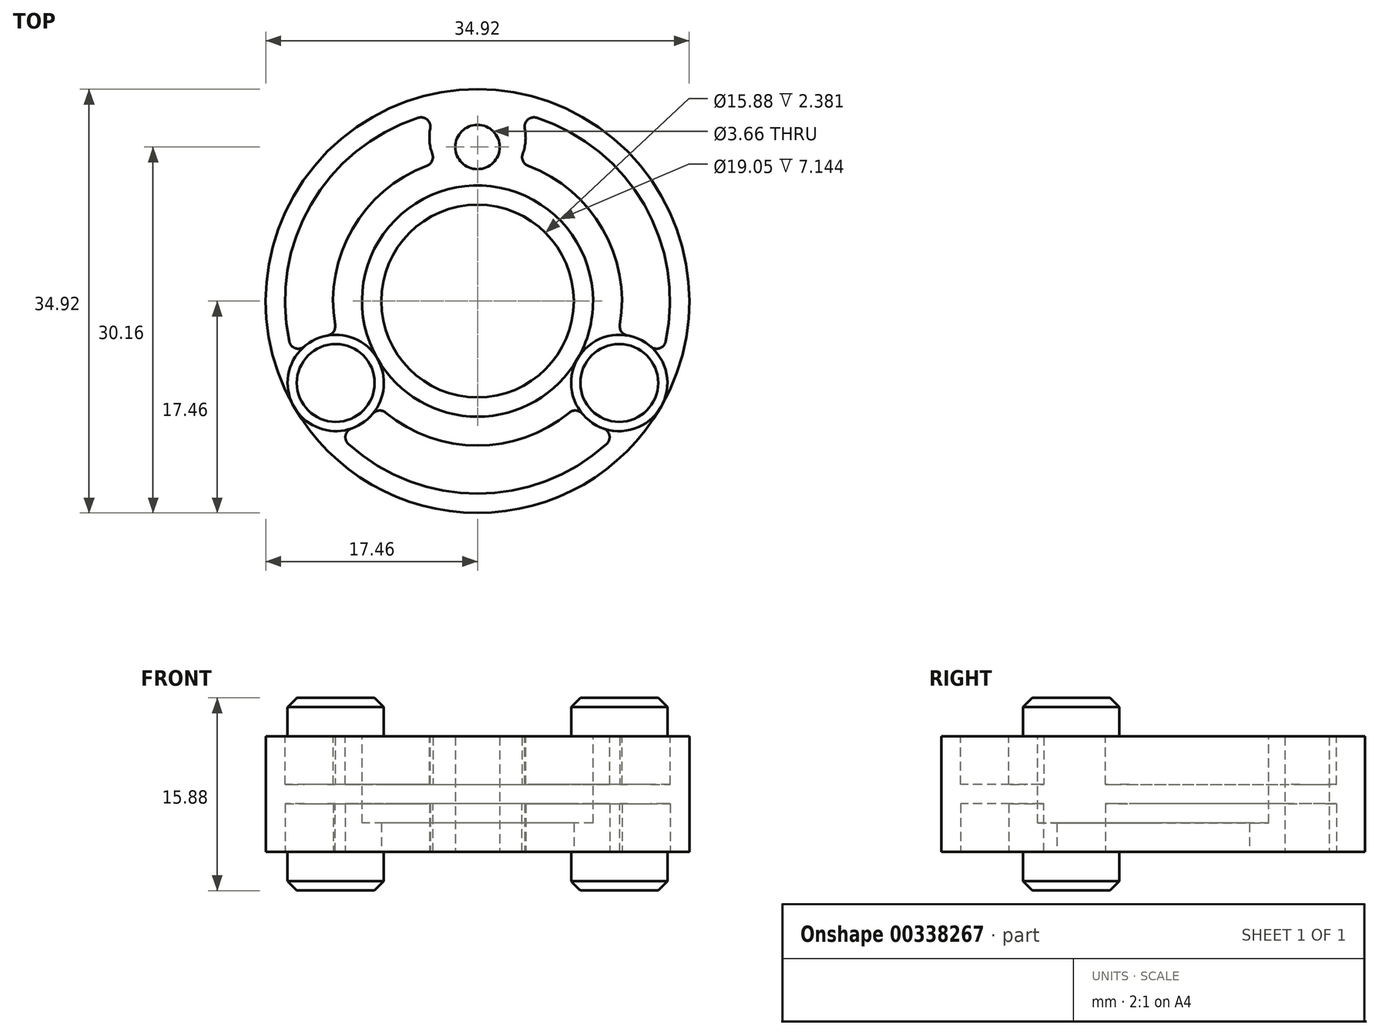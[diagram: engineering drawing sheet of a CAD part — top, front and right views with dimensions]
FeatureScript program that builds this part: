
annotation { "Feature Type Name" : "Feature", "Feature Type Description" : "" }
export const myFeature = defineFeature(function(context is Context, id is Id, definition is map)
    precondition{}
    {
        {
            var Q0;
            Q0=qCreatedBy(makeId("Top.planeOp"),FACE);
            var sketch = newSketch(context, id + "F0", { "sketchPlane" : qUnion([Q0])});
            skCircle(sketch, "E0", {"center": v(0, 0) * mm, "radius": 7.94 * mm});
            skCircle(sketch, "E1", {"center": v(0, 0) * mm, "radius": 17.46 * mm});
            skLineSegment(sketch, "E2", {"start": v(0, 0) * mm, "end": v(0, 12.7) * mm, "construction": true});
            skCircle(sketch, "E3", {"center": v(0, 12.7) * mm, "radius": 4.76 * mm, "construction": true});
            skCircle(sketch, "E4", {"center": v(0, 12.7) * mm, "radius": 1.83 * mm});
            skSolve(sketch);
        }
        {
            var Q0;
            Q0 = qSketchRegion(id + "F0", true);
            extrude(context, id + "F1", {"entities" : qUnion([Q0]), "depth" : 9.52 * mm});
        }
        {
            var Q0;
            Q0=makeQuery(id+"F1.opExtrude","CAP_FACE",FACE,{"disambiguationData":[OSD([sQuery(id+"F0.wireOp",EDGE,"E0"),sQuery(id+"F0.wireOp",EDGE,"E1"),sQuery(id+"F0.wireOp",EDGE,"E4")])],"isStart":false});
            var sketch = newSketch(context, id + "F2", { "sketchPlane" : qUnion([Q0])});
            skCircle(sketch, "E5", {"center": v(0, 0) * mm, "radius": 9.53 * mm});
            skSolve(sketch);
        }
        {
            var Q0;
            Q0 = qSketchRegion(id + "F2", true);
            extrude(context, id + "F3", {"entities" : qUnion([Q0]), "operationType" : NewBodyOperationType.REMOVE, "oppositeDirection" : true, "depth" : 7.14 * mm});
        }
        {
            var Q0;
            {var subQ0=sQuery(id+"F0.wireOp",EDGE,"E1");var subQ1=makeQuery(id+"F1.opExtrude","CAP_FACE",FACE,{"disambiguationData":[OSD([sQuery(id+"F0.wireOp",EDGE,"E0"),subQ0,sQuery(id+"F0.wireOp",EDGE,"E4")])],"isStart":false});Q0=makeQuery(id+"FaGNQa3NOKQJJ3d_1.boolean.opBoolean","SPLIT",FACE,{"disambiguationData":[TD([subQ1,makeQuery(id+"F1.opExtrude","SWEPT_FACE",FACE,{"disambiguationData":[OSD([subQ0])]}),makeQuery(id+"F3.boolean.opBoolean","COPY",FACE,{"derivedFrom":makeQuery(id+"F3.opExtrude","SWEPT_FACE",FACE,{"disambiguationData":[OSD([sQuery(id+"F2.wireOp",EDGE,"E5")])]})}),makeQuery(id+"FaGNQa3NOKQJJ3d_1.opExtrude","SWEPT_FACE",FACE,{"disambiguationData":[OSD([sQuery(id+"FimIUrEkqtjUp3z_1.wireOp",EDGE,"HlGXKecl-ggte-uXjZ-GF2z-oe2yHpBcJ9Dq")])]}),makeQuery(id+"FaGNQa3NOKQJJ3d_1.opExtrude","SWEPT_FACE",FACE,{"disambiguationData":[OSD([sQuery(id+"FimIUrEkqtjUp3z_1.wireOp",EDGE,"b06J7RxP-un1X-OzPm-o8VI-wkIMPVGFyDBE")])]})])],"derivedFrom":subQ1});}
            var sketch = newSketch(context, id + "F4", { "sketchPlane" : qUnion([Q0])});
            skArc(sketch, "E6", {"start": v(-3.42, 15.5) * mm, "mid": v(-3.97, 13.45) * mm, "end": v(-3.38, 11.42) * mm});
            skArc(sketch, "E7", {"start": v(-3.38, 11.42) * mm, "mid": v(-10.31, 5.95) * mm, "end": v(-11.58, -2.78) * mm});
            skArc(sketch, "E8", {"start": v(-3.42, 15.5) * mm, "mid": v(-13.75, 7.94) * mm, "end": v(-15.14, -4.79) * mm});
            skLineSegment(sketch, "E9", {"start": v(0, 0) * mm, "end": v(0, 13.5) * mm, "construction": true});
            skArc(sketch, "E10", {"start": v(-11.58, -2.78) * mm, "mid": v(-13.63, -3.29) * mm, "end": v(-15.14, -4.79) * mm});
            skArc(sketch, "E11", {"start": v(-15.14, -4.79) * mm, "mid": v(-9.74, -10.2) * mm, "end": v(-11.58, -2.78) * mm, "construction": true});
            skLineSegment(sketch, "E12", {"start": v(-11.69, -6.75) * mm, "end": v(0, 0) * mm, "construction": true});
            skSolve(sketch);
        }
        {
            var Q0;
            Q0 = qSketchRegion(id + "F4", true);
            extrude(context, id + "F5", {"entities" : qUnion([Q0]), "operationType" : NewBodyOperationType.REMOVE, "oppositeDirection" : true, "depth" : 3.97 * mm});
        }
        {
            var Q0;
            Q0=makeQuery(id+"F1.opExtrude","CAP_FACE",FACE,{"disambiguationData":[OSD([sQuery(id+"F0.wireOp",EDGE,"E0"),sQuery(id+"F0.wireOp",EDGE,"E1"),sQuery(id+"F0.wireOp",EDGE,"E4")])],"isStart":true});
            var sketch = newSketch(context, id + "F6", { "sketchPlane" : qUnion([Q0])});
            skArc(sketch, "E13", {"start": v(-15.14, 4.79) * mm, "mid": v(-13.75, -7.94) * mm, "end": v(-3.42, -15.5) * mm});
            skArc(sketch, "E14", {"start": v(-11.58, 2.78) * mm, "mid": v(-10.31, -5.95) * mm, "end": v(-3.38, -11.42) * mm});
            skArc(sketch, "E15", {"start": v(-15.14, 4.79) * mm, "mid": v(-13.63, 3.29) * mm, "end": v(-11.58, 2.78) * mm});
            skArc(sketch, "E16", {"start": v(-3.38, -11.42) * mm, "mid": v(-3.97, -13.45) * mm, "end": v(-3.42, -15.5) * mm});
            skSolve(sketch);
        }
        {
            var Q0;
            Q0 = qSketchRegion(id + "F6", true);
            extrude(context, id + "F7", {"entities" : qUnion([Q0]), "operationType" : NewBodyOperationType.REMOVE, "oppositeDirection" : true, "depth" : 3.97 * mm});
        }
        {
            var Q0;
            Q0=makeQuery(id+"F5.boolean.opBoolean","COPY",EDGE,{"derivedFrom":makeQuery(id+"F5.opExtrude","SWEPT_EDGE",EDGE,{"disambiguationData":[OSD([sQuery(id+"F4.wireOp",EDGE,"E8"),sQuery(id+"F4.wireOp",EDGE,"E10")])]})});
            var Q1;
            Q1=makeQuery(id+"F5.boolean.opBoolean","COPY",EDGE,{"derivedFrom":makeQuery(id+"F5.opExtrude","SWEPT_EDGE",EDGE,{"disambiguationData":[OSD([sQuery(id+"F4.wireOp",EDGE,"E7"),sQuery(id+"F4.wireOp",EDGE,"E10")])]})});
            var Q2;
            Q2=makeQuery(id+"F5.boolean.opBoolean","COPY",EDGE,{"derivedFrom":makeQuery(id+"F5.opExtrude","SWEPT_EDGE",EDGE,{"disambiguationData":[OSD([sQuery(id+"F4.wireOp",EDGE,"E6"),sQuery(id+"F4.wireOp",EDGE,"E7")])]})});
            var Q3;
            Q3=makeQuery(id+"F5.boolean.opBoolean","COPY",EDGE,{"derivedFrom":makeQuery(id+"F5.opExtrude","SWEPT_EDGE",EDGE,{"disambiguationData":[OSD([sQuery(id+"F4.wireOp",EDGE,"E6"),sQuery(id+"F4.wireOp",EDGE,"E8")])]})});
            var Q4;
            Q4=makeQuery(id+"F7.boolean.opBoolean","COPY",EDGE,{"derivedFrom":makeQuery(id+"F7.opExtrude","SWEPT_EDGE",EDGE,{"disambiguationData":[OSD([sQuery(id+"F6.wireOp",EDGE,"E14"),sQuery(id+"F6.wireOp",EDGE,"E16")])]})});
            var Q5;
            Q5=makeQuery(id+"F7.boolean.opBoolean","COPY",EDGE,{"derivedFrom":makeQuery(id+"F7.opExtrude","SWEPT_EDGE",EDGE,{"disambiguationData":[OSD([sQuery(id+"F6.wireOp",EDGE,"E13"),sQuery(id+"F6.wireOp",EDGE,"E16")])]})});
            var Q6;
            Q6=makeQuery(id+"F7.boolean.opBoolean","COPY",EDGE,{"derivedFrom":makeQuery(id+"F7.opExtrude","SWEPT_EDGE",EDGE,{"disambiguationData":[OSD([sQuery(id+"F6.wireOp",EDGE,"E14"),sQuery(id+"F6.wireOp",EDGE,"E15")])]})});
            var Q7;
            Q7=makeQuery(id+"F7.boolean.opBoolean","COPY",EDGE,{"derivedFrom":makeQuery(id+"F7.opExtrude","SWEPT_EDGE",EDGE,{"disambiguationData":[OSD([sQuery(id+"F6.wireOp",EDGE,"E13"),sQuery(id+"F6.wireOp",EDGE,"E15")])]})});
            fillet(context, id + "F8", {"entities" : qUnion([Q0, Q1, Q2, Q3, Q4, Q5, Q6, Q7]), "radius" : 0.76 * mm, "tangentPropagation" : true, "allowEdgeOverflow" : false});
        }
        {
            var Q0;
            Q0=makeQuery(id+"F8.opFillet","BLEND_FACE",FACE,{"disambiguationData":[OSD([sQuery(id+"F4.wireOp",EDGE,"E8"),sQuery(id+"F4.wireOp",EDGE,"E10")])]});
            var Q1;
            Q1=makeQuery(id+"F5.boolean.opBoolean","COPY",FACE,{"derivedFrom":makeQuery(id+"F5.opExtrude","SWEPT_FACE",FACE,{"disambiguationData":[OSD([sQuery(id+"F4.wireOp",EDGE,"E10")])]})});
            var Q2;
            Q2=makeQuery(id+"F8.opFillet","BLEND_FACE",FACE,{"disambiguationData":[OSD([sQuery(id+"F4.wireOp",EDGE,"E7"),sQuery(id+"F4.wireOp",EDGE,"E10")])]});
            var Q3;
            Q3=makeQuery(id+"F5.boolean.opBoolean","COPY",FACE,{"derivedFrom":makeQuery(id+"F5.opExtrude","SWEPT_FACE",FACE,{"disambiguationData":[OSD([sQuery(id+"F4.wireOp",EDGE,"E7")])]})});
            var Q4;
            Q4=makeQuery(id+"F8.opFillet","BLEND_FACE",FACE,{"disambiguationData":[OSD([sQuery(id+"F4.wireOp",EDGE,"E6"),sQuery(id+"F4.wireOp",EDGE,"E7")])]});
            var Q5;
            Q5=makeQuery(id+"F5.boolean.opBoolean","COPY",FACE,{"derivedFrom":makeQuery(id+"F5.opExtrude","SWEPT_FACE",FACE,{"disambiguationData":[OSD([sQuery(id+"F4.wireOp",EDGE,"E6")])]})});
            var Q6;
            Q6=makeQuery(id+"F8.opFillet","BLEND_FACE",FACE,{"disambiguationData":[OSD([sQuery(id+"F4.wireOp",EDGE,"E6"),sQuery(id+"F4.wireOp",EDGE,"E8")])]});
            var Q7;
            Q7=makeQuery(id+"F5.boolean.opBoolean","COPY",FACE,{"derivedFrom":makeQuery(id+"F5.opExtrude","SWEPT_FACE",FACE,{"disambiguationData":[OSD([sQuery(id+"F4.wireOp",EDGE,"E8")])]})});
            var Q8;
            Q8=makeQuery(id+"F8.opFillet","BLEND_FACE",FACE,{"disambiguationData":[OSD([sQuery(id+"F6.wireOp",EDGE,"E13"),sQuery(id+"F6.wireOp",EDGE,"E15")])]});
            var Q9;
            Q9=makeQuery(id+"F7.boolean.opBoolean","COPY",FACE,{"derivedFrom":makeQuery(id+"F7.opExtrude","SWEPT_FACE",FACE,{"disambiguationData":[OSD([sQuery(id+"F6.wireOp",EDGE,"E15")])]})});
            var Q10;
            Q10=makeQuery(id+"F8.opFillet","BLEND_FACE",FACE,{"disambiguationData":[OSD([sQuery(id+"F6.wireOp",EDGE,"E14"),sQuery(id+"F6.wireOp",EDGE,"E15")])]});
            var Q11;
            Q11=makeQuery(id+"F7.boolean.opBoolean","COPY",FACE,{"derivedFrom":makeQuery(id+"F7.opExtrude","SWEPT_FACE",FACE,{"disambiguationData":[OSD([sQuery(id+"F6.wireOp",EDGE,"E14")])]})});
            var Q12;
            Q12=makeQuery(id+"F8.opFillet","BLEND_FACE",FACE,{"disambiguationData":[OSD([sQuery(id+"F6.wireOp",EDGE,"E14"),sQuery(id+"F6.wireOp",EDGE,"E16")])]});
            var Q13;
            Q13=makeQuery(id+"F7.boolean.opBoolean","COPY",FACE,{"derivedFrom":makeQuery(id+"F7.opExtrude","SWEPT_FACE",FACE,{"disambiguationData":[OSD([sQuery(id+"F6.wireOp",EDGE,"E16")])]})});
            var Q14;
            Q14=makeQuery(id+"F8.opFillet","BLEND_FACE",FACE,{"disambiguationData":[OSD([sQuery(id+"F6.wireOp",EDGE,"E13"),sQuery(id+"F6.wireOp",EDGE,"E16")])]});
            var Q15;
            Q15=makeQuery(id+"F7.boolean.opBoolean","COPY",FACE,{"derivedFrom":makeQuery(id+"F7.opExtrude","SWEPT_FACE",FACE,{"disambiguationData":[OSD([sQuery(id+"F6.wireOp",EDGE,"E13")])]})});
            var Q16;
            Q16=makeQuery(id+"F5.boolean.opBoolean","COPY",FACE,{"derivedFrom":makeQuery(id+"F5.opExtrude","CAP_FACE",FACE,{"disambiguationData":[OSD([sQuery(id+"F4.wireOp",EDGE,"E6"),sQuery(id+"F4.wireOp",EDGE,"E7"),sQuery(id+"F4.wireOp",EDGE,"E8"),sQuery(id+"F4.wireOp",EDGE,"E10")])],"isStart":false})});
            var Q17;
            Q17=makeQuery(id+"F7.boolean.opBoolean","COPY",FACE,{"derivedFrom":makeQuery(id+"F7.opExtrude","CAP_FACE",FACE,{"disambiguationData":[OSD([sQuery(id+"F6.wireOp",EDGE,"E13"),sQuery(id+"F6.wireOp",EDGE,"E14"),sQuery(id+"F6.wireOp",EDGE,"E15"),sQuery(id+"F6.wireOp",EDGE,"E16")])],"isStart":false})});
            var Q18;
            Q18=makeQuery(id+"F1.opExtrude","SWEPT_FACE",FACE,{"disambiguationData":[OSD([sQuery(id+"F0.wireOp",EDGE,"E0")])]});
            circularPattern(context, id + "F9", {"patternType" : PatternType.FACE, "faces" : qUnion([Q0, Q1, Q2, Q3, Q4, Q5, Q6, Q7, Q8, Q9, Q10, Q11, Q12, Q13, Q14, Q15, Q16, Q17]), "axis" : qUnion([Q18]), "angle" : 360 * degree, "instanceCount" : 3, "equalSpace" : true});
        }
        {
            var Q0;
            Q0=makeQuery(id+"F1.opExtrude","CAP_FACE",FACE,{"disambiguationData":[OSD([sQuery(id+"F0.wireOp",EDGE,"E0"),sQuery(id+"F0.wireOp",EDGE,"E1"),sQuery(id+"F0.wireOp",EDGE,"E4")])],"isStart":true});
            var sketch = newSketch(context, id + "F10", { "sketchPlane" : qUnion([Q0])});
            skCircle(sketch, "E17", {"center": v(11.69, 6.75) * mm, "radius": 3.97 * mm});
            skCircle(sketch, "E18", {"center": v(-11.69, 6.75) * mm, "radius": 3.97 * mm});
            skSolve(sketch);
        }
        {
            var Q0;
            Q0 = qSketchRegion(id + "F10", true);
            extrude(context, id + "F11", {"entities" : qUnion([Q0]), "operationType" : NewBodyOperationType.ADD, "depth" : 3.17 * mm, "hasSecondDirection" : true, "secondDirectionOppositeDirection" : true, "secondDirectionDepth" : 12.7 * mm});
        }
        {
            var Q0;
            Q0=makeQuery(id+"F11.opExtrude","CAP_EDGE",EDGE,{"disambiguationData":[OSD([sQuery(id+"F10.wireOp",EDGE,"E18")])],"isStart":true});
            var Q1;
            Q1=makeQuery(id+"F11.opExtrude","CAP_EDGE",EDGE,{"disambiguationData":[OSD([sQuery(id+"F10.wireOp",EDGE,"E17")])],"isStart":true});
            var Q2;
            Q2=makeQuery(id+"F11.opExtrude","CAP_EDGE",EDGE,{"disambiguationData":[OSD([sQuery(id+"F10.wireOp",EDGE,"E17")])],"isStart":false});
            var Q3;
            Q3=makeQuery(id+"F11.opExtrude","CAP_EDGE",EDGE,{"disambiguationData":[OSD([sQuery(id+"F10.wireOp",EDGE,"E18")])],"isStart":false});
            chamfer(context, id + "F12", {"entities" : qUnion([Q0, Q1, Q2, Q3]), "width" : 0.76 * mm, "tangentPropagation" : true});
        }
    });
